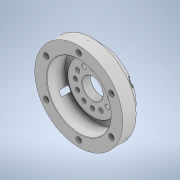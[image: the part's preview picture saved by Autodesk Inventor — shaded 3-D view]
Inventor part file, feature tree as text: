
AUTODESK INVENTOR PART (.ipt)
format: ipt  version: 2020 (Build 240168000, 168)  size: 477,184 bytes
history: native  units: in
note: dims shown in document units (in); Inventor stores cm internally (conversion verified against a paired STEP export)
features: extrude x8, sketch x8, chamfer x2, plane x1, projected_geometry x1
ambient origin geometry x8: Origin, YZ Plane, XZ Plane, XY Plane, X Axis, Y Axis, Z Axis, Center Point
bodies: Solid1 (feature_tree)
feature tree (20):
  extrude  "Extrusion1"  Depth=1.23in TaperAngle=0.0deg
  extrude  "Extrusion2"  Depth=3.51in
  extrude  "Extrusion3"  Depth=0.5in TaperAngle=0.0deg
  chamfer  "Chamfer1"  Distance=0.5in Angle=45.0deg
  plane  "Work Plane1"
  extrude  "Extrusion4"  Depth=2.0625in
  extrude  "Extrusion5"  Depth=0.2656in
  extrude  "Extrusion6"  Depth=0.4375in
  chamfer  "Chamfer2"  Distance=1.1811in Angle=360.0deg
  extrude  "Extrusion7"  Depth=0.69in
  extrude  "Extrusion8"  Depth=0.0118in
  sketch  "Sketch1"  dims[d0=4.825in d1=1.23in d2=0.0in]
  sketch  "Sketch2"  dims[d3=2.74in d4=3.51in]
  sketch  "Sketch3"  dims[d5=0.99in d6=0.0in d7=0.75in d8=0.0in d9=0.5in d10=0.125in d11=45.0deg]
  projected_geometry  "Projected Loop1"
  sketch  "Sketch5"  dims[d12=-0.5in d13=2.0625in]
  sketch  "Sketch6"  dims[d14=2.3622in d16=360.0deg d18=0.2656in]
  sketch  "Sketch8"  dims[d19=0.5in d20=0.0in d21=0.4375in d22=1.1811in d24=360.0deg]
  sketch  "Sketch9"  dims[d26=0.0in d27=0.0in d28=0.69in]
  sketch  "Sketch10"  dims[d29=1.1811in d31=360.0deg d33=1.126in d34=0.2031in d35=0.9375in d36=4.7244in d38=360.0deg d40=0.0in d41=0.0in d42=0.025in d43=0.125in d44=45.0deg d45=2.3622in d47=360.0deg d49=0.0118in d50=0.0in d51=2.3622in d53=360.0deg d55=0.0118in d56=0.0in]
